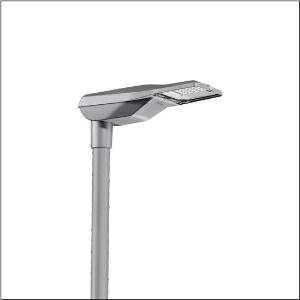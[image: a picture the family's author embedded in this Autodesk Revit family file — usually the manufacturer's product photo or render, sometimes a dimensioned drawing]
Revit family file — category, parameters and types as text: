
# Revit family: streetlight_sl_21_iq_micro___st1_5a_5xe1p31d08db_ec34
name_source: partatom
category: Lighting Fixtures
units: mm (PartAtom-declared; Revit-internal decimal feet)

## family parameters
Cut with Voids When Loaded = No
Host = Face
Light Source = No
Part Type = Normal
Room Calculation Point = No
Round Connector Dimension = Use Diameter
Shared = No

## types (1)
- --- (1 x LED, 4730 lm, 36.4 W, 3000K)
    Apparent Load = 36 VA
    CIE Flux Codes = 22 53 95 100 100
    Color Rendering = 70
    Color Temperature = 3000K
    Default Elevation = 1800 mm
    Description = Streetlight SL 21 iQ micro, mast luminaire, primary light control with lens, of PMMA, primary optical cover: cover, of toughened safety glass, transparent, light distribution: ST1.5a, light emission: direct distribution, primary light characteristic: asymmetric, installation type: post-top, side-entry, LED, High Power LED, rated luminous flux: 4.730lm, luminous efficacy: 130lm/W, light colour: 730, colour temperature: 3000K, control: Auto-Match, Temp-Guard, Lumen-Switch, Night-Set, Smart-Wire, Light-Fading, Desk-Remote (wireless, voltage-free reading and setting of iQ features in the workshop via application-optimized NFC function/RFID function), optimised constant luminous flux control (CLO 2.0), presetting dimming linear, mains connection: 220..240V, AC, 50/60Hz, start of lifetime: 36W, end of service life: 38W, reduction: 16W, luminaire housing, of diecast aluminium, powder-coated, Siteco® metallic grey (DB 702S), corrosivity category C5 mid according to DIN EN ISO 12944, please order mast flange separately, inclination adjustable: 0°, 5°, 10°, 15°, sealing non-destructively replaceable, multi-level sealing system, length: 528mm, width: 235mm, height: 110mm, mast flange for spigot size: 42mm (side-entry): 5XC10008XM4, 60/48mm (side-entry/post-top): 5XC10108XM2, 76/60mm (side-entry/post-top): 5XC10108XM1, protection rating (complete): IP66, insulation class (complete): insulation class II (safety insulation), certification: CE, ENEC, ENEC+, VDE, impact resistance: IK09, permissible operating ambient temperature for outdoor applications: -40..+50°C, standard-compliant lighting for roads and squares, packaging unit: 1 piece

Light Distribution: ST1.5a
    Height = 110 mm
    Lamp = 1 x LED
    Lamp Light Flux = 4730 lm
    Lamp Power = 36.4 W
    Lamp count = 1
    Length = 528 mm
    Luminous efficacy = 130 lm/W
    Manufacturer = Siteco
    ModVariant = No
    Model = 5XE1P31D08DB
    Number of Poles = 1
    OnlyDefault = Yes
    Power Factor = 1
    Product Name = Streetlight SL 21 iQ micro | ST1.5a
    Product group = mast luminaire | pylon top
    ProductGroupID = 6100
    Protection Class = Protection class II
    Protection Degree = IP 66
    RLX_Detail_Level = 1
    RLX_Emergency_Light_Flux = 0 lm
    RLX_Emergency_Type = 0
    RLX_Emergency_Type_DB = No
    RlxData = <blob elided: 103437 chars, md5=ee9adcd0>
    Socket = socket
    Standby Power = 0 W
    System Light Flux = 4730 lm
    System Power = 36 W
    Type Comments = factory setting: luminous flux: 100 % | dim-lin: 254 | 715 mA
    Type Image = l_1006881.jpg
    URL = http://relux.com
    VarID = @adj_104057
    Voltage = 0 V
    Weight = 0.00 kg
    Width = 235 mm

## geometry (parser evidence)
native form markers: Blend x4, Sweep x11
no freeform markers — native parametric forms only
